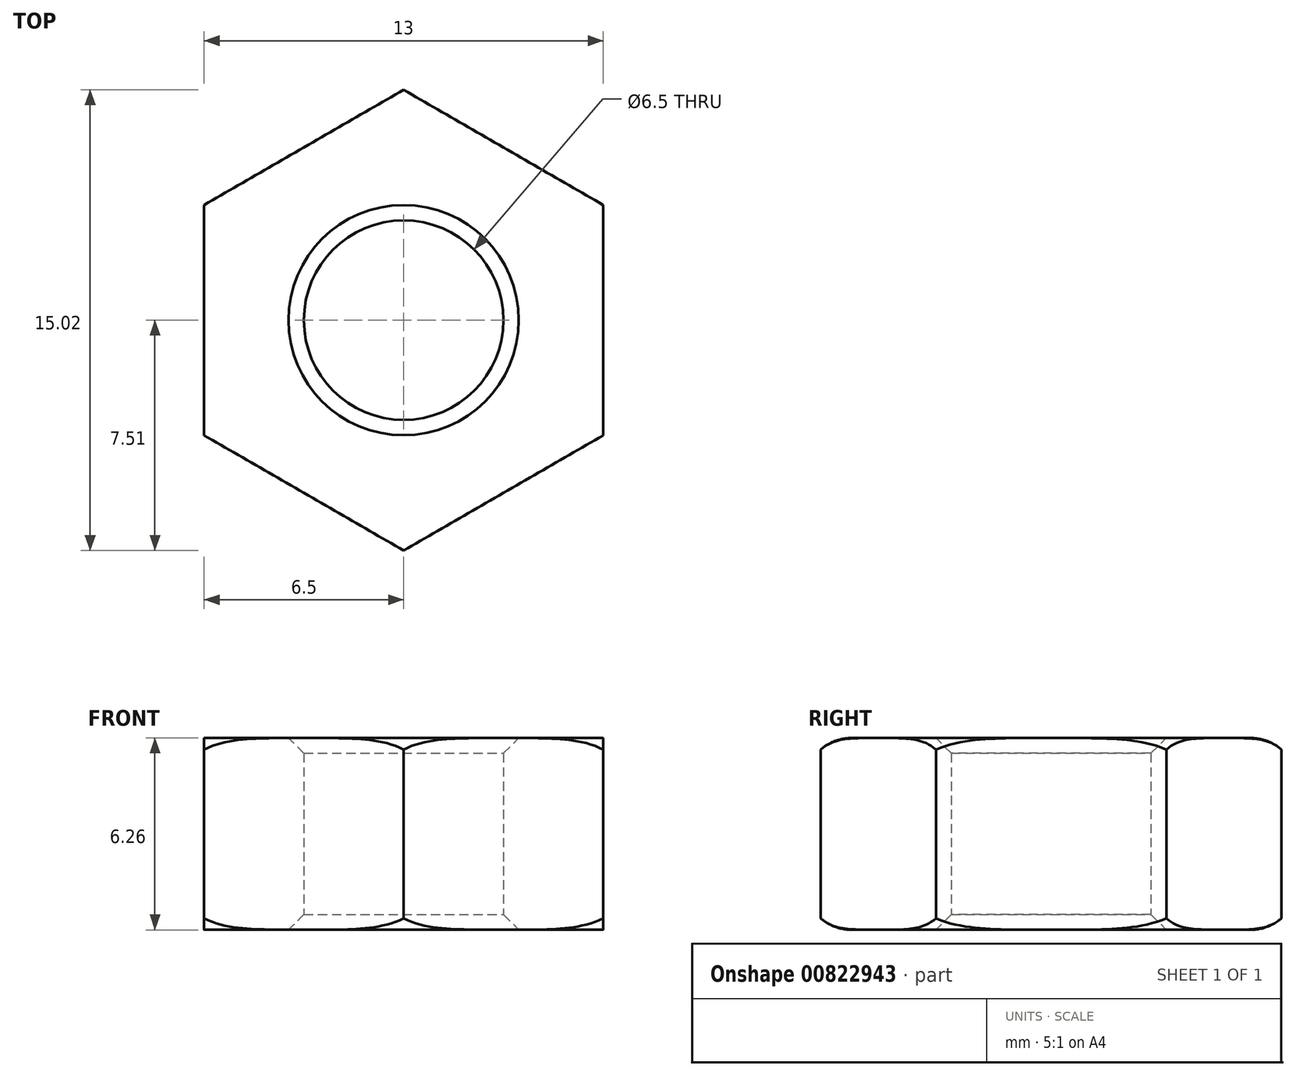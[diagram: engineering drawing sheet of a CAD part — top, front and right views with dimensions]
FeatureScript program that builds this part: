
annotation { "Feature Type Name" : "Feature", "Feature Type Description" : "" }
export const myFeature = defineFeature(function(context is Context, id is Id, definition is map)
    precondition{}
    {
        {
            var Q0;
            Q0=qCreatedBy(makeId("Front.planeOp"),FACE);
            var sketch = newSketch(context, id + "F0", { "sketchPlane" : qUnion([Q0])});
            skLineSegment(sketch, "E0", {"start": v(-3.25, 0) * mm, "end": v(-3.25, 2.63) * mm});
            skLineSegment(sketch, "E1", {"start": v(-3.25, 2.63) * mm, "end": v(-3.75, 3.12) * mm});
            skLineSegment(sketch, "E2", {"start": v(-3.75, 3.13) * mm, "end": v(-6.5, 3.13) * mm});
            skLineSegment(sketch, "E3", {"start": v(-6.5, 3.13) * mm, "end": v(-7.5, 2.75) * mm, "construction": true});
            skLineSegment(sketch, "E4", {"start": v(-7.5, 2.75) * mm, "end": v(-7.5, 0) * mm});
            skLineSegment(sketch, "E5", {"start": v(0, 0) * mm, "end": v(0, 8.86) * mm, "construction": true});
            skLineSegment(sketch, "E6", {"start": v(0, 0) * mm, "end": v(-3.25, 0) * mm, "construction": true});
            skLineSegment(sketch, "E7.MirrorCS", {"start": v(-3.25, -2.63) * mm, "end": v(-3.75, -3.12) * mm});
            skLineSegment(sketch, "E8.MirrorCS", {"start": v(-7.5, -2.75) * mm, "end": v(-7.5, 0) * mm});
            skLineSegment(sketch, "E9.MirrorCS", {"start": v(-7.5, 0) * mm, "end": v(-3.25, 0) * mm, "construction": true});
            skLineSegment(sketch, "E10.MirrorCS", {"start": v(-3.75, -3.12) * mm, "end": v(-6.5, -3.12) * mm});
            skLineSegment(sketch, "E11.MirrorCS", {"start": v(-6.5, -3.12) * mm, "end": v(-7.5, -2.75) * mm, "construction": true});
            skLineSegment(sketch, "E12.MirrorCS", {"start": v(-3.25, 0) * mm, "end": v(-3.25, -2.63) * mm});
            skLineSegment(sketch, "E13", {"start": v(-6.5, 3.12) * mm, "end": v(-6.5, -3.12) * mm, "construction": true});
            skCircle(sketch, "E14", {"center": v(0, 0) * mm, "radius": 6.5 * mm, "construction": true});
            skLineSegment(sketch, "E15", {"start": v(0, 0) * mm, "end": v(-10.5, -6.06) * mm, "construction": true});
            skLineSegment(sketch, "E16.0", {"start": v(-3.75, -6.5) * mm, "end": v(-7.5, 0) * mm, "construction": true});
            skLineSegment(sketch, "E16.1", {"start": v(-7.5, 0) * mm, "end": v(-3.75, 6.5) * mm, "construction": true});
            skLineSegment(sketch, "E16.2", {"start": v(-3.75, 6.5) * mm, "end": v(3.75, 6.5) * mm, "construction": true});
            skLineSegment(sketch, "E16.3", {"start": v(3.75, 6.5) * mm, "end": v(7.5, 0) * mm, "construction": true});
            skLineSegment(sketch, "E16.4", {"start": v(7.5, 0) * mm, "end": v(3.75, -6.5) * mm, "construction": true});
            skLineSegment(sketch, "E16.5", {"start": v(3.75, -6.5) * mm, "end": v(-3.75, -6.5) * mm, "construction": true});
            skPoint(sketch, "E16.0.midPoint", {"position": v(-5.63, -3.25) * mm});
            skArc(sketch, "E17", {"start": v(-6.5, 3.13) * mm, "mid": v(-7.04, 3.03) * mm, "end": v(-7.5, 2.75) * mm});
            skArc(sketch, "E18.MirrorCS", {"start": v(-6.5, -3.13) * mm, "mid": v(-7.04, -3.03) * mm, "end": v(-7.5, -2.75) * mm});
            skSolve(sketch);
        }
        {
            var Q0;
            Q0=makeQuery(id+"F0.imprint","IMPRINT",FACE,{"disambiguationData":[TD([[makeQuery(id+"F0.imprint","IMPRINT",EDGE,{"derivedFrom":sQuery(id+"F0.wireOp",EDGE,"E0")}),1.0]])]});
            var Q1;
            Q1=sQuery(id+"F0.wireOp",EDGE,"E5");
            revolve(context, id + "F1", {"surfaceOperationType" : NewSurfaceOperationType.NEW, "entities" : qUnion([Q0]), "axis" : qUnion([Q1]), "revolveType" : RevolveType.FULL});
        }
        {
            var Q0;
            Q0=qCreatedBy(makeId("Top.planeOp"),FACE);
            var sketch = newSketch(context, id + "F2", { "sketchPlane" : qUnion([Q0])});
            skCircle(sketch, "E19", {"center": v(0, 0) * mm, "radius": 6.5 * mm, "construction": true});
            skLineSegment(sketch, "E20", {"start": v(0, 0) * mm, "end": v(-1.01, 0) * mm, "construction": true});
            skLineSegment(sketch, "E21", {"start": v(0, 0) * mm, "end": v(6.5, 0) * mm, "construction": true});
            skLineSegment(sketch, "E22.0", {"start": v(6.5, 3.75) * mm, "end": v(6.5, -3.75) * mm});
            skLineSegment(sketch, "E22.1", {"start": v(6.5, -3.75) * mm, "end": v(0, -7.5) * mm});
            skLineSegment(sketch, "E22.2", {"start": v(0, -7.5) * mm, "end": v(-6.5, -3.75) * mm});
            skLineSegment(sketch, "E22.3", {"start": v(-6.5, -3.75) * mm, "end": v(-6.5, 3.75) * mm});
            skLineSegment(sketch, "E22.4", {"start": v(-6.5, 3.75) * mm, "end": v(0, 7.5) * mm});
            skLineSegment(sketch, "E22.5", {"start": v(0, 7.5) * mm, "end": v(6.5, 3.75) * mm});
            skPoint(sketch, "E22.0.midPoint", {"position": v(6.5, 0) * mm});
            skCircle(sketch, "E23", {"center": v(0, 0) * mm, "radius": 8.53 * mm});
            skSolve(sketch);
        }
        {
            var Q0;
            Q0 = qSketchRegion(id + "F2", true);
            extrude(context, id + "F3", {"entities" : qUnion([Q0]), "operationType" : NewBodyOperationType.REMOVE, "endBound" : BoundingType.SYMMETRIC, "oppositeDirection" : true, "depth" : 25 * mm, "offsetDistance" : 25 * mm});
        }
    });
